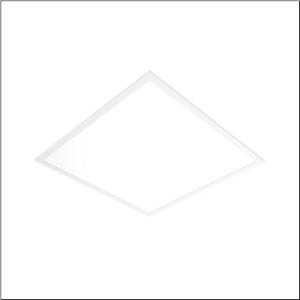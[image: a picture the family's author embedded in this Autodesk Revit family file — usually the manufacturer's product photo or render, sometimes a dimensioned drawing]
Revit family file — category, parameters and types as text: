
# Revit family: apollon_r__41_51mh12h72443_9ce2
name_source: partatom
category: Lighting Fixtures
units: mm (PartAtom-declared; Revit-internal decimal feet)

## family parameters
Cut with Voids When Loaded = No
Host = Face
Light Source = No
Part Type = Normal
Room Calculation Point = No
Round Connector Dimension = Use Diameter
Shared = No

## types (1)
- Apollon® 41 (1 x LED, 5000 lm, 38.5 W, 4000K)
    Apparent Load = 39 VA
    CIE Flux Codes = 61 87 97 100 100
    Color Rendering = 80
    Color Temperature = 4000K
    Default Elevation = 1800 mm
    Description = Apollon® 41, office luminaire, primary optical cover: prismatic diffuser, of PS, light emission: direct distribution, primary light characteristic: symmetric, installation type: lay-in mounting, LED, rated luminous flux: 5.000lm, luminous efficacy: 130lm/W, light colour: 840, colour temperature: 4000K, with terminal, 3-pole, mains connection: 220..240V, AC, 50/60Hz, rated input power: 38.5W, housing, of aluminium section, traffic white (RAL 9016), module: M600, length: 600mm, width: 600mm, height: 28mm, housing upper side, of sheet steel, protection rating (complete): IP20, protection rating (lamp compartment, on room side): IP40, insulation class (complete): insulation class II (safety insulation), certification: CE, ENEC, permissible operating ambient temperature: -25..+40°C, packaging unit: 1 piece
    Height = 0 mm  [stored 0 ft]
    Lamp = 1 x LED
    Lamp Light Flux = 5000 lm
    Lamp Power = 38.5 W
    Lamp count = 1
    Length = 600 mm
    Luminous efficacy = 130 lm/W
    Manufacturer = Siteco
    ModVariant = No
    Model = 51MH12H72443
    Mounting Place = Ceiling
    Mounting Type = Recessed
    Number of Poles = 1
    OnlyDefault = Yes
    Power Factor = 1
    Product Name = Apollon® 41
    Product group = office luminaire | ceiling recessed
    ProductGroupID = 400
    Protection Class = Protection class II
    Protection Degree = IP 20
    RLX_Detail_Level = 1
    RLX_Emergency_Light_Flux = 0 lm
    RLX_Emergency_Type = 0
    RLX_Emergency_Type_DB = No
    RlxData = <blob elided: 12197 chars, md5=c94fb76e>
    Socket = socket
    Standby Power = 0 W
    System Light Flux = 5000 lm
    System Power = 39 W
    Type Comments = Product without accessories
    Type Image = l_1291024.jpg
    URL = http://relux.com
    VarID = ---
    Voltage = 0 V
    Weight = 0.00 kg
    Width = 600 mm

note: [stored X ft] marks values corroborated as IEEE doubles in the binary element streams (Revit-internal decimal feet)

## geometry (parser evidence)
native form markers: Sweep x10
no freeform markers — native parametric forms only
